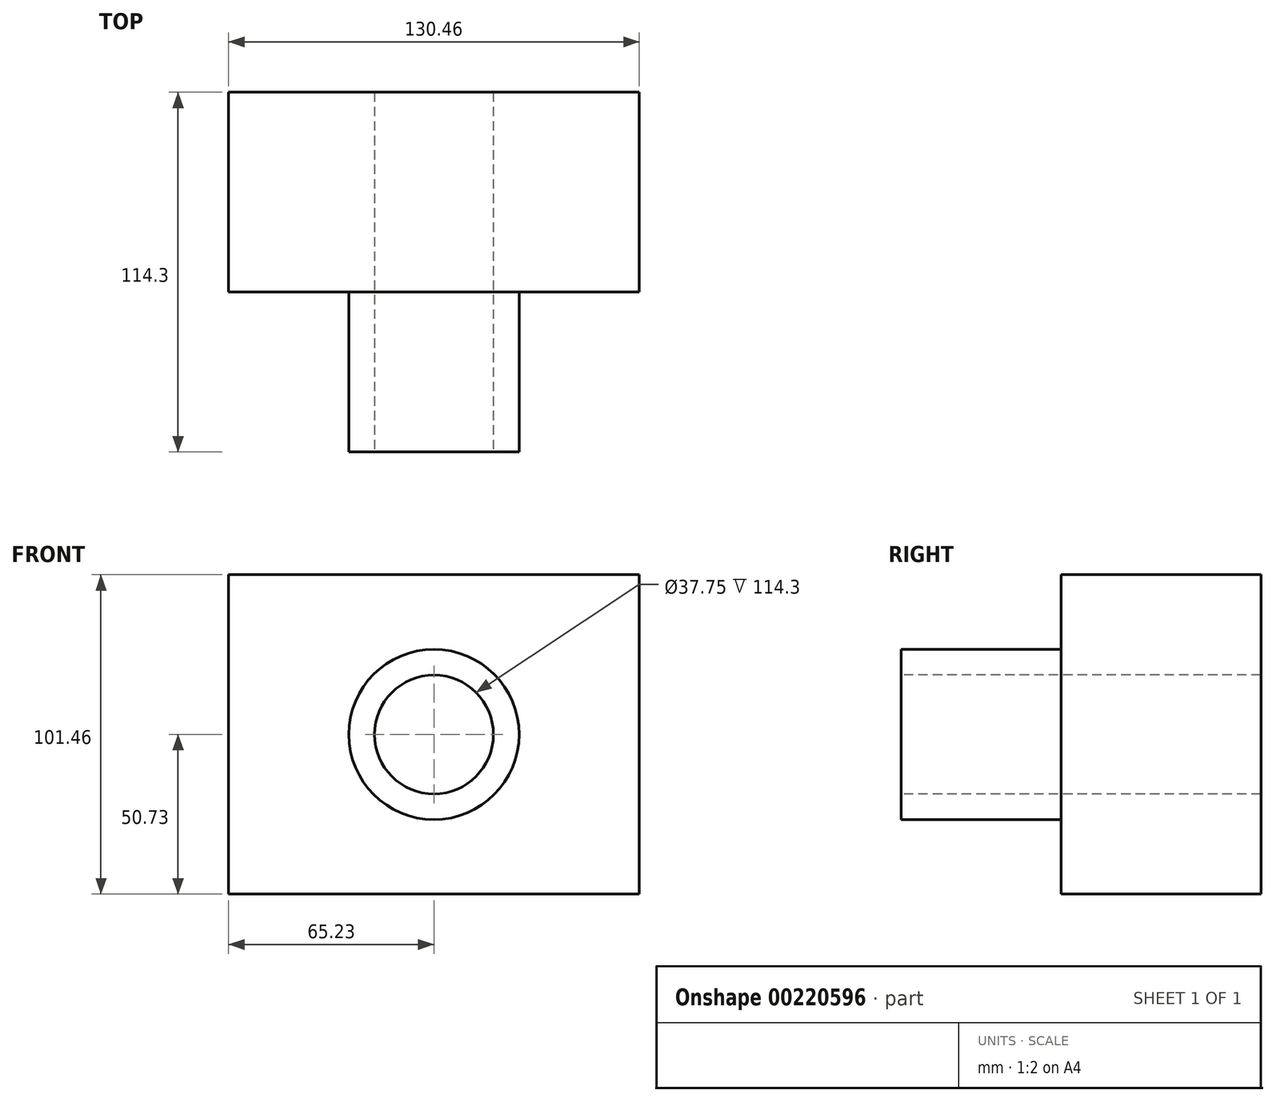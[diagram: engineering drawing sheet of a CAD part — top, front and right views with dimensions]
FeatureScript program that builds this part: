
annotation { "Feature Type Name" : "Feature", "Feature Type Description" : "" }
export const myFeature = defineFeature(function(context is Context, id is Id, definition is map)
    precondition{}
    {
        {
            var Q0;
            Q0=qCreatedBy(makeId("Front.planeOp"),FACE);
            var sketch = newSketch(context, id + "F0", { "sketchPlane" : qUnion([Q0])});
            skLineSegment(sketch, "E0.bottom", {"start": v(-65.23, 50.73) * mm, "end": v(65.23, 50.73) * mm});
            skLineSegment(sketch, "E0.top", {"start": v(-65.23, -50.73) * mm, "end": v(65.23, -50.73) * mm});
            skLineSegment(sketch, "E0.left", {"start": v(-65.23, 50.73) * mm, "end": v(-65.23, -50.73) * mm});
            skLineSegment(sketch, "E0.right", {"start": v(65.23, 50.73) * mm, "end": v(65.23, -50.73) * mm});
            skPoint(sketch, "E0.middle", {"position": v(0, 0) * mm});
            skSolve(sketch);
        }
        {
            var Q0;
            Q0=makeQuery(id+"F0.imprint","IMPRINT",FACE,{"disambiguationData":[TD([[makeQuery(id+"F0.imprint","IMPRINT",EDGE,{"derivedFrom":sQuery(id+"F0.wireOp",EDGE,"E0.bottom")}),-1.0]])]});
            extrude(context, id + "F1", {"entities" : qUnion([Q0]), "depth" : 63.5 * mm});
        }
        {
            var Q0;
            Q0=makeQuery(id+"F1.opExtrude","CAP_FACE",FACE,{"disambiguationData":[OSD([sQuery(id+"F0.wireOp",EDGE,"E0.bottom"),sQuery(id+"F0.wireOp",EDGE,"E0.top"),sQuery(id+"F0.wireOp",EDGE,"E0.left"),sQuery(id+"F0.wireOp",EDGE,"E0.right")])],"isStart":false});
            var sketch = newSketch(context, id + "F2", { "sketchPlane" : qUnion([Q0])});
            skCircle(sketch, "E1", {"center": v(0, 0) * mm, "radius": 27.04 * mm});
            skSolve(sketch);
        }
        {
            var Q0;
            Q0=makeQuery(id+"F2.imprint","IMPRINT",FACE,{"disambiguationData":[TD([[makeQuery(id+"F2.imprint","IMPRINT",EDGE,{"derivedFrom":sQuery(id+"F2.wireOp",EDGE,"E1")}),1.0]])]});
            extrude(context, id + "F3", {"entities" : qUnion([Q0]), "operationType" : NewBodyOperationType.ADD, "depth" : 50.8 * mm});
        }
        {
            var Q0;
            Q0=makeQuery(id+"F3.opExtrude","CAP_FACE",FACE,{"disambiguationData":[OSD([sQuery(id+"F2.wireOp",EDGE,"E1")])],"isStart":false});
            var sketch = newSketch(context, id + "F4", { "sketchPlane" : qUnion([Q0])});
            skCircle(sketch, "E2", {"center": v(0, 0) * mm, "radius": 18.88 * mm});
            skSolve(sketch);
        }
        {
            var Q0;
            Q0=makeQuery(id+"F4.imprint","IMPRINT",FACE,{"disambiguationData":[TD([[makeQuery(id+"F4.imprint","IMPRINT",EDGE,{"derivedFrom":sQuery(id+"F4.wireOp",EDGE,"E2")}),1.0]])]});
            extrude(context, id + "F5", {"entities" : qUnion([Q0]), "operationType" : NewBodyOperationType.REMOVE, "oppositeDirection" : true, "depth" : 179.58 * mm});
        }
    });
